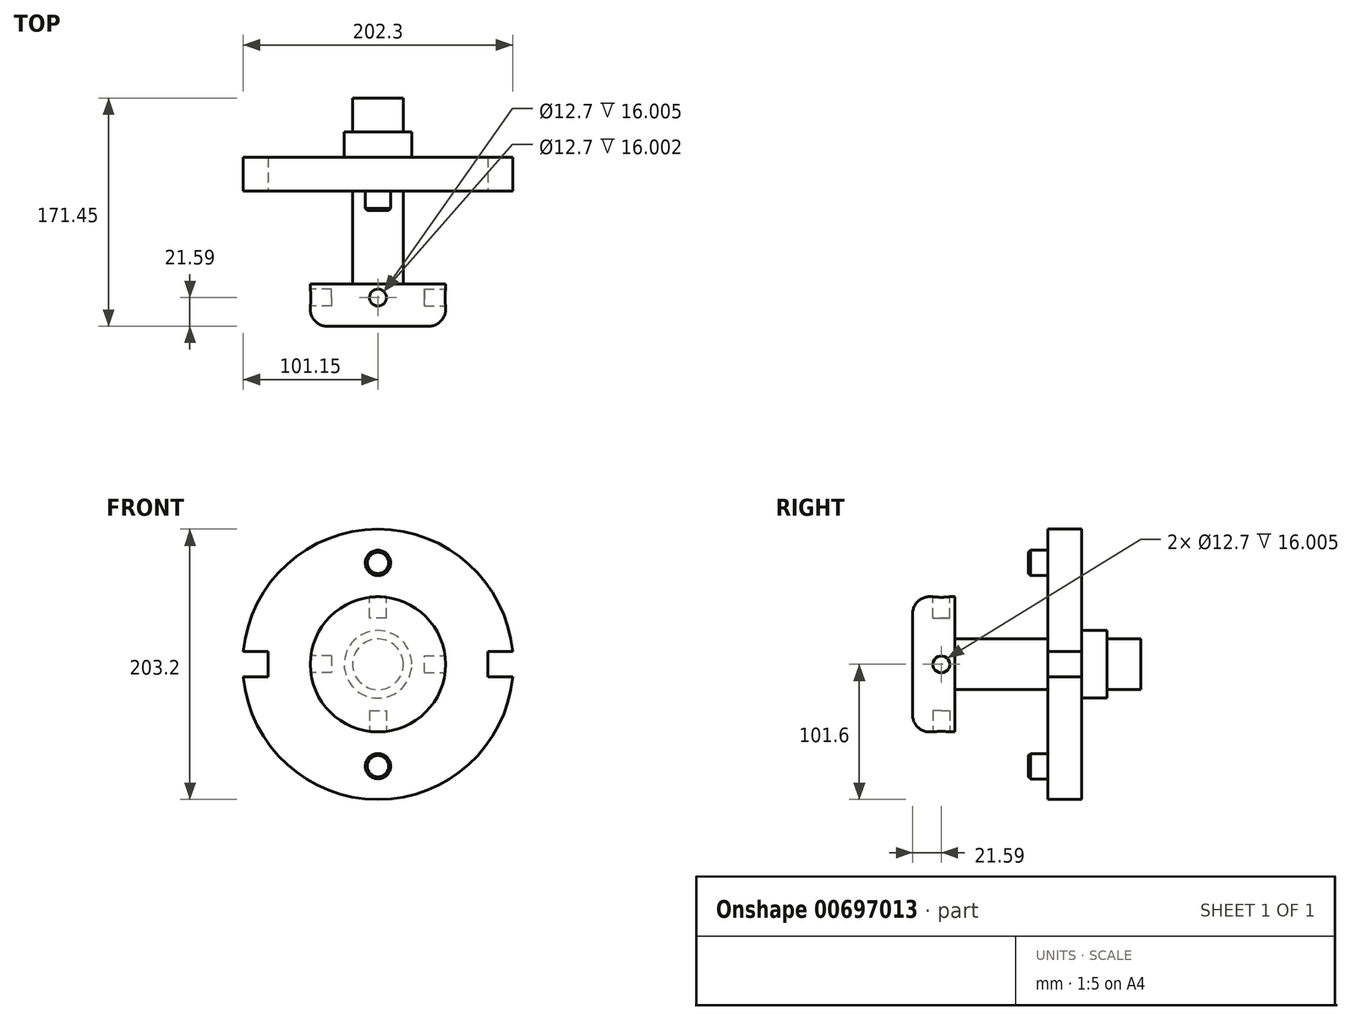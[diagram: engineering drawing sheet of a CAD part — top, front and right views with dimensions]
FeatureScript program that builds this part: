
annotation { "Feature Type Name" : "Feature", "Feature Type Description" : "" }
export const myFeature = defineFeature(function(context is Context, id is Id, definition is map)
    precondition{}
    {
        {
            var Q0;
            Q0=qCreatedBy(makeId("Front.planeOp"),FACE);
            var sketch = newSketch(context, id + "F0", { "sketchPlane" : qUnion([Q0])});
            skCircle(sketch, "E0", {"center": v(0, 0) * mm, "radius": 101.6 * mm});
            skSolve(sketch);
        }
        {
            var Q0;
            Q0=qSketchRegion(id+"F0",true);
            extrude(context, id + "F1", {"entities" : qUnion([Q0]), "depth" : 19.05 * mm});
        }
        {
            var Q0;
            Q0=makeQuery(id+"F1.opExtrude","CAP_FACE",FACE,{"disambiguationData":[OSD([sQuery(id+"F0.wireOp",EDGE,"E0")])],"isStart":false});
            var sketch = newSketch(context, id + "F2", { "sketchPlane" : qUnion([Q0])});
            skCircle(sketch, "E1", {"center": v(0, 0) * mm, "radius": 19.05 * mm});
            skSolve(sketch);
        }
        {
            var Q0;
            Q0=qSketchRegion(id+"F2",true);
            var Q1;
            Q1=makeQuery(id+"F2.imprint","IMPRINT",FACE,{"disambiguationData":[TD([[makeQuery(id+"F2.imprint","IMPRINT",EDGE,{"derivedFrom":sQuery(id+"F2.wireOp",EDGE,"E1")}),1.0]])]});
            extrude(context, id + "F3", {"entities" : qUnion([Q0, Q1]), "operationType" : NewBodyOperationType.ADD, "depth" : 76.2 * mm});
        }
        {
            var Q0;
            Q0=makeQuery(id+"F3.opExtrude","CAP_FACE",FACE,{"disambiguationData":[OSD([sQuery(id+"F2.wireOp",EDGE,"E1")])],"isStart":false});
            var sketch = newSketch(context, id + "F4", { "sketchPlane" : qUnion([Q0])});
            skCircle(sketch, "E2", {"center": v(0, 0) * mm, "radius": 50.8 * mm});
            skSolve(sketch);
        }
        {
            var Q0;
            Q0=makeQuery(id+"F4.imprint","IMPRINT",FACE,{"disambiguationData":[TD([[makeQuery(id+"F4.imprint","IMPRINT",EDGE,{"derivedFrom":sQuery(id+"F4.wireOp",EDGE,"E2")}),1.0]])]});
            var Q1;
            Q1=makeQuery(id+"F4.imprint","IMPRINT",FACE,{"disambiguationData":[TD([[makeQuery(id+"F4.imprint","IMPRINT",EDGE,{"derivedFrom":makeQuery(id+"F3.opExtrude","CAP_EDGE",EDGE,{"disambiguationData":[OSD([sQuery(id+"F2.wireOp",EDGE,"E1")])],"isStart":false})}),1.0]])]});
            extrude(context, id + "F5", {"entities" : qUnion([Q0, Q1]), "operationType" : NewBodyOperationType.ADD, "depth" : 31.75 * mm});
        }
        {
            var Q0;
            Q0=makeQuery(id+"F1.opExtrude","CAP_FACE",FACE,{"disambiguationData":[OSD([sQuery(id+"F0.wireOp",EDGE,"E0")])],"isStart":false});
            var sketch = newSketch(context, id + "F6", { "sketchPlane" : qUnion([Q0])});
            skCircle(sketch, "E3", {"center": v(0, 76.2) * mm, "radius": 9.53 * mm});
            skCircle(sketch, "E4", {"center": v(0, -76.58) * mm, "radius": 9.52 * mm});
            skSolve(sketch);
        }
        {
            var Q0;
            Q0=qSketchRegion(id+"F6",true);
            extrude(context, id + "F7", {"entities" : qUnion([Q0]), "operationType" : NewBodyOperationType.ADD, "depth" : 20.83 * mm});
        }
        {
            var Q0;
            Q0=makeQuery(id+"F5.opExtrude","CAP_EDGE",EDGE,{"disambiguationData":[OSD([sQuery(id+"F4.wireOp",EDGE,"E2")])],"isStart":false});
            fillet(context, id + "F8", {"entities" : qUnion([Q0]), "radius" : 12.7 * mm, "tangentPropagation" : true, "allowEdgeOverflow" : false});
        }
        {
            var Q0;
            Q0=makeQuery(id+"F1.opExtrude","CAP_FACE",FACE,{"disambiguationData":[OSD([sQuery(id+"F0.wireOp",EDGE,"E0")])],"isStart":true});
            var sketch = newSketch(context, id + "F9", { "sketchPlane" : qUnion([Q0])});
            skCircle(sketch, "E5", {"center": v(0, 0) * mm, "radius": 25.4 * mm});
            skSolve(sketch);
        }
        {
            var Q0;
            Q0=qSketchRegion(id+"F9",true);
            extrude(context, id + "F10", {"entities" : qUnion([Q0]), "operationType" : NewBodyOperationType.ADD, "depth" : 19.05 * mm});
        }
        {
            var Q0;
            Q0=makeQuery(id+"F10.opExtrude","CAP_FACE",FACE,{"disambiguationData":[OSD([sQuery(id+"F9.wireOp",EDGE,"E5")])],"isStart":false});
            var sketch = newSketch(context, id + "F11", { "sketchPlane" : qUnion([Q0])});
            skCircle(sketch, "E6", {"center": v(0, 0) * mm, "radius": 19.05 * mm});
            skSolve(sketch);
        }
        {
            var Q0;
            Q0=makeQuery(id+"F11.imprint","IMPRINT",FACE,{"disambiguationData":[TD([[makeQuery(id+"F11.imprint","IMPRINT",EDGE,{"derivedFrom":sQuery(id+"F11.wireOp",EDGE,"E6")}),1.0]])]});
            extrude(context, id + "F12", {"entities" : qUnion([Q0]), "operationType" : NewBodyOperationType.ADD, "depth" : 25.4 * mm});
        }
        {
            var Q0;
            Q0=qSketchRegion(id+"F0",true);
            extrude(context, id + "F13", {"entities" : qUnion([Q0]), "operationType" : NewBodyOperationType.ADD, "depth" : 25.4 * mm});
        }
        {
            var Q0;
            Q0=makeQuery(id+"F13.opExtrude","CAP_FACE",FACE,{"disambiguationData":[OSD([sQuery(id+"F0.wireOp",EDGE,"E0")])],"isStart":false});
            var sketch = newSketch(context, id + "F14", { "sketchPlane" : qUnion([Q0])});
            skLineSegment(sketch, "E7", {"start": v(0, 0) * mm, "end": v(82.55, 0) * mm});
            skLineSegment(sketch, "E8", {"start": v(82.55, 0) * mm, "end": v(82.55, 9.53) * mm});
            skLineSegment(sketch, "E9", {"start": v(82.55, 0) * mm, "end": v(82.55, -9.53) * mm});
            skLineSegment(sketch, "E10", {"start": v(82.55, -9.53) * mm, "end": v(120.55, -9.53) * mm});
            skLineSegment(sketch, "E11", {"start": v(120.55, -9.53) * mm, "end": v(120.55, 9.53) * mm});
            skLineSegment(sketch, "E12", {"start": v(120.55, 9.53) * mm, "end": v(82.55, 9.53) * mm});
            skSolve(sketch);
        }
        {
            var Q0;
            {var subQ0=sQuery(id+"F14.wireOp",EDGE,"E11");Q0=makeQuery(id+"F14.imprint","IMPRINT",FACE,{"disambiguationData":[TD([[makeQuery(id+"F14.imprint","IMPRINT",EDGE,{"derivedFrom":subQ0}),1.0]])]});}
            var Q1;
            {var subQ5=sQuery(id+"F14.wireOp",EDGE,"E8");Q1=makeQuery(id+"F14.imprint","IMPRINT",FACE,{"disambiguationData":[TD([[makeQuery(id+"F14.imprint","IMPRINT",EDGE,{"derivedFrom":subQ5}),-1.0]])]});}
            var Q2;
            Q2=sQuery(id+"F14.wireOp",EDGE,"E10");
            var Q3;
            Q3=sQuery(id+"F14.wireOp",EDGE,"E12");
            var Q4;
            Q4=sQuery(id+"F14.wireOp",EDGE,"E9");
            var Q5;
            Q5=sQuery(id+"F14.wireOp",EDGE,"E11");
            var Q6;
            Q6=sQuery(id+"F14.wireOp",EDGE,"E8");
            extrude(context, id + "F15", {"entities" : qUnion([Q0, Q1]), "operationType" : NewBodyOperationType.REMOVE, "surfaceEntities" : qUnion([Q2, Q3, Q4, Q5, Q6]), "oppositeDirection" : true, "depth" : 27.94 * mm});
        }
        {
            var Q0;
            Q0=makeQuery(id+"F13.opExtrude","CAP_FACE",FACE,{"disambiguationData":[OSD([sQuery(id+"F0.wireOp",EDGE,"E0")])],"isStart":false});
            var sketch = newSketch(context, id + "F16", { "sketchPlane" : qUnion([Q0])});
            skLineSegment(sketch, "E13", {"start": v(0, 0) * mm, "end": v(-82.55, 0) * mm});
            skLineSegment(sketch, "E14", {"start": v(-82.55, 0) * mm, "end": v(-82.55, 9.52) * mm});
            skLineSegment(sketch, "E15", {"start": v(-82.55, 0) * mm, "end": v(-82.55, -9.53) * mm});
            skLineSegment(sketch, "E16", {"start": v(-82.55, -9.53) * mm, "end": v(-117.5, -9.53) * mm});
            skLineSegment(sketch, "E17", {"start": v(-117.5, -9.53) * mm, "end": v(-117.5, 9.52) * mm});
            skLineSegment(sketch, "E18", {"start": v(-117.5, 9.52) * mm, "end": v(-82.55, 9.52) * mm});
            skSolve(sketch);
        }
        {
            var Q0;
            {var subQ0=sQuery(id+"F16.wireOp",EDGE,"E17");Q0=makeQuery(id+"F16.imprint","IMPRINT",FACE,{"disambiguationData":[TD([[makeQuery(id+"F16.imprint","IMPRINT",EDGE,{"derivedFrom":subQ0}),-1.0]])]});}
            var Q1;
            {var subQ5=sQuery(id+"F16.wireOp",EDGE,"E14");Q1=makeQuery(id+"F16.imprint","IMPRINT",FACE,{"disambiguationData":[TD([[makeQuery(id+"F16.imprint","IMPRINT",EDGE,{"derivedFrom":subQ5}),1.0]])]});}
            extrude(context, id + "F17", {"entities" : qUnion([Q0, Q1]), "operationType" : NewBodyOperationType.REMOVE, "oppositeDirection" : true, "depth" : 25.4 * mm});
        }
        {
            var Q0;
            Q0=makeQuery(id+"F7.opExtrude","CAP_EDGE",EDGE,{"disambiguationData":[OSD([sQuery(id+"F6.wireOp",EDGE,"E3")])],"isStart":false});
            var Q1;
            Q1=makeQuery(id+"F7.opExtrude","CAP_EDGE",EDGE,{"disambiguationData":[OSD([sQuery(id+"F6.wireOp",EDGE,"E4")])],"isStart":false});
            chamfer(context, id + "F18", {"entities" : qUnion([Q0, Q1]), "chamferType" : ChamferType.OFFSET_ANGLE, "width" : 1.52 * mm, "oppositeDirection" : false, "angle" : 45 * degree, "tangentPropagation" : true});
        }
        {
            var Q0;
            Q0=qCreatedBy(makeId("Top.planeOp"),FACE);
            cPlane(context, id + "F19", {"entities" : qUnion([Q0]), "cplaneType" : CPlaneType.OFFSET, "offset" : 50.8 * mm, "width" : 152.4 * mm, "height" : 152.4 * mm});
        }
        {
            var Q0;
            Q0=qCreatedBy(id+"F19.planeOp",FACE);
            var sketch = newSketch(context, id + "F20", { "sketchPlane" : qUnion([Q0])});
            skCircle(sketch, "E19", {"center": v(0, -105.4) * mm, "radius": 6.35 * mm});
            skSolve(sketch);
        }
        {
            var Q0;
            Q0=qSketchRegion(id+"F20",true);
            extrude(context, id + "F21", {"entities" : qUnion([Q0]), "operationType" : NewBodyOperationType.REMOVE, "oppositeDirection" : true, "depth" : 16 * mm});
        }
        {
            var Q0;
            Q0=qCreatedBy(id+"F19.planeOp",FACE);
            cPlane(context, id + "F22", {"entities" : qUnion([Q0]), "cplaneType" : CPlaneType.OFFSET, "offset" : 101.6 * mm, "oppositeDirection" : true, "width" : 152.4 * mm, "height" : 152.4 * mm});
        }
        {
            var Q0;
            Q0=qCreatedBy(id+"F22.planeOp",FACE);
            var sketch = newSketch(context, id + "F23", { "sketchPlane" : qUnion([Q0])});
            skLineSegment(sketch, "E20", {"start": v(0, 0) * mm, "end": v(0, -105.4) * mm});
            skCircle(sketch, "E21", {"center": v(0, -105.4) * mm, "radius": 6.35 * mm});
            skSolve(sketch);
        }
        {
            var Q0;
            Q0=qSketchRegion(id+"F23",true);
            extrude(context, id + "F24", {"entities" : qUnion([Q0]), "operationType" : NewBodyOperationType.REMOVE, "depth" : 16 * mm});
        }
        {
            var Q0;
            Q0=qCreatedBy(makeId("Right.planeOp"),FACE);
            cPlane(context, id + "F25", {"entities" : qUnion([Q0]), "cplaneType" : CPlaneType.OFFSET, "offset" : 50.8 * mm, "width" : 152.4 * mm, "height" : 152.4 * mm});
        }
        {
            var Q0;
            Q0=qCreatedBy(id+"F25.planeOp",FACE);
            var sketch = newSketch(context, id + "F26", { "sketchPlane" : qUnion([Q0])});
            skLineSegment(sketch, "E22", {"start": v(0, 0) * mm, "end": v(-105.41, 0) * mm});
            skCircle(sketch, "E23", {"center": v(-105.41, 0) * mm, "radius": 6.35 * mm});
            skSolve(sketch);
        }
        {
            var Q0;
            Q0=qSketchRegion(id+"F26",true);
            extrude(context, id + "F27", {"entities" : qUnion([Q0]), "operationType" : NewBodyOperationType.REMOVE, "oppositeDirection" : true, "depth" : 16 * mm});
        }
        {
            var Q0;
            Q0=qCreatedBy(makeId("Right.planeOp"),FACE);
            cPlane(context, id + "F28", {"entities" : qUnion([Q0]), "cplaneType" : CPlaneType.OFFSET, "offset" : 50.8 * mm, "oppositeDirection" : true, "width" : 152.4 * mm, "height" : 152.4 * mm});
        }
        {
            var Q0;
            Q0=qCreatedBy(id+"F28.planeOp",FACE);
            var sketch = newSketch(context, id + "F29", { "sketchPlane" : qUnion([Q0])});
            skLineSegment(sketch, "E24", {"start": v(0, 0) * mm, "end": v(-105.41, 0) * mm});
            skCircle(sketch, "E25", {"center": v(-105.41, 0) * mm, "radius": 6.35 * mm});
            skSolve(sketch);
        }
        {
            var Q0;
            Q0=qSketchRegion(id+"F29",true);
            extrude(context, id + "F30", {"entities" : qUnion([Q0]), "operationType" : NewBodyOperationType.REMOVE, "depth" : 16 * mm});
        }
    });
